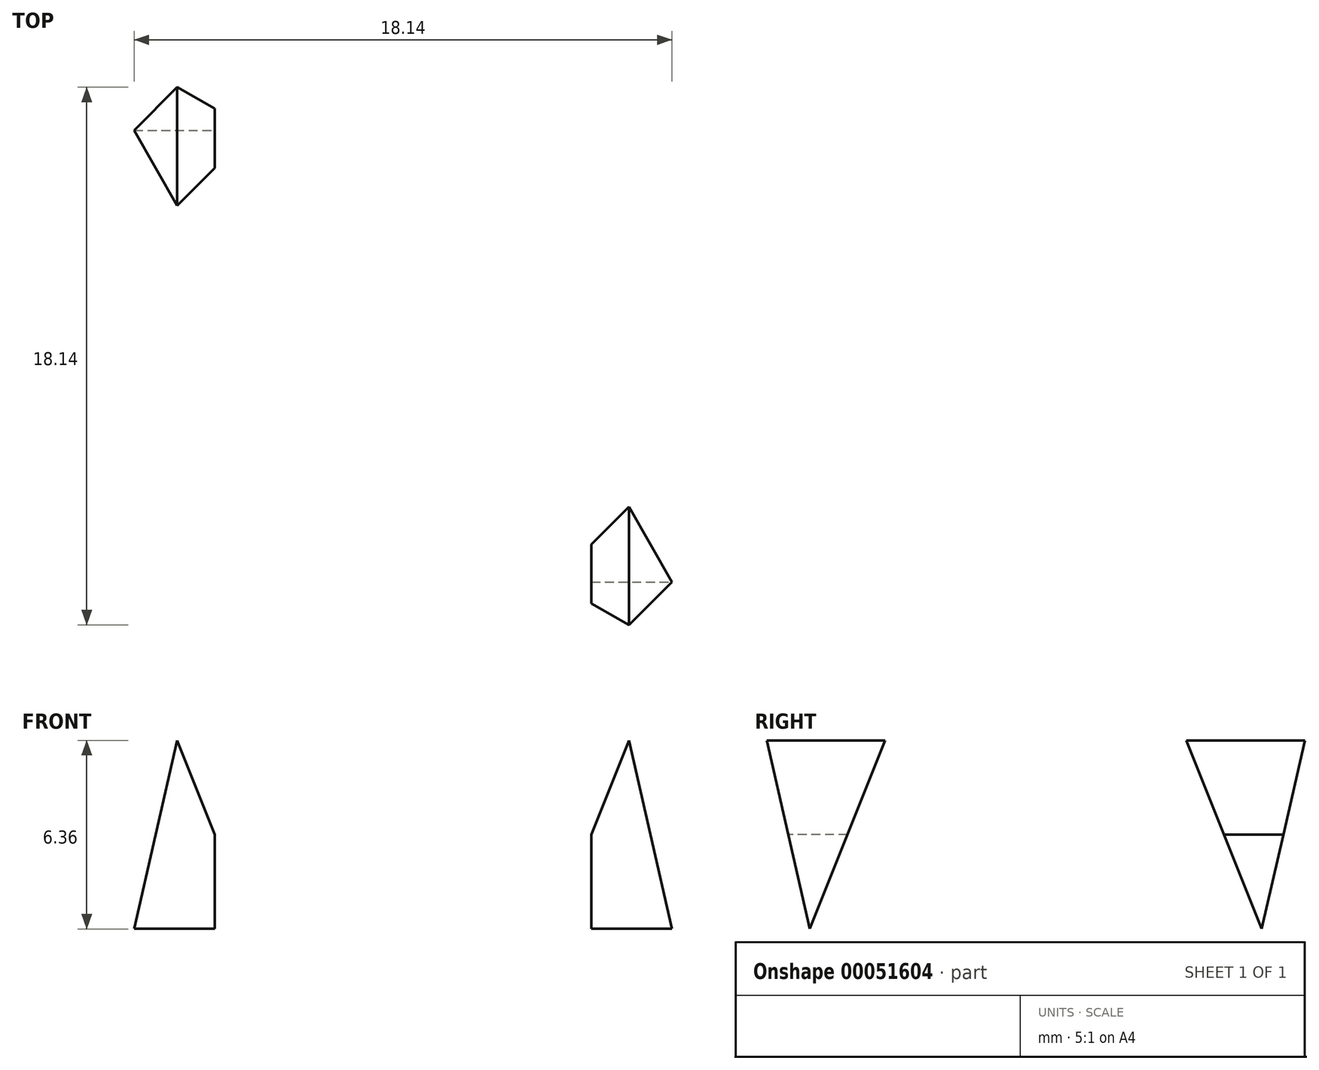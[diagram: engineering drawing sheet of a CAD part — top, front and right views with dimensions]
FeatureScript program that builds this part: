
annotation { "Feature Type Name" : "Feature", "Feature Type Description" : "" }
export const myFeature = defineFeature(function(context is Context, id is Id, definition is map)
    precondition{}
    {
        {
            var Q0;
            Q0=qCreatedBy(makeId("Front.planeOp"),FACE);
            var sketch = newSketch(context, id + "F0", { "sketchPlane" : qUnion([Q0])});
            skLineSegment(sketch, "E0", {"start": v(0, 0) * mm, "end": v(0, 38.1) * mm});
            skLineSegment(sketch, "E1", {"start": v(0, 38.1) * mm, "end": v(38.1, 38.1) * mm});
            skLineSegment(sketch, "E2", {"start": v(38.1, 38.1) * mm, "end": v(38.1, 0) * mm});
            skLineSegment(sketch, "E3", {"start": v(0, 0) * mm, "end": v(38.1, 0) * mm});
            skSolve(sketch);
        }
        {
            var Q0;
            Q0=makeQuery(id+"F0.imprint","IMPRINT",FACE,{"disambiguationData":[TD([[makeQuery(id+"F0.imprint","IMPRINT",EDGE,{"derivedFrom":sQuery(id+"F0.wireOp",EDGE,"E0")}),-1.0]])]});
            extrude(context, id + "F1", {"entities" : qUnion([Q0]), "depth" : 38.1 * mm});
        }
        {
            var Q0;
            Q0=qCreatedBy(makeId("Front.planeOp"),FACE);
            cPlane(context, id + "F2", {"entities" : qUnion([Q0]), "cplaneType" : CPlaneType.OFFSET, "offset" : 38.1 * mm, "width" : 152.4 * mm, "height" : 152.4 * mm});
        }
        {
            var Q0;
            Q0=qCreatedBy(makeId("Right.planeOp"),FACE);
            cPlane(context, id + "F3", {"entities" : qUnion([Q0]), "cplaneType" : CPlaneType.OFFSET, "offset" : 38.1 * mm, "width" : 152.4 * mm, "height" : 152.4 * mm});
        }
        {
            var Q0;
            Q0=qCreatedBy(makeId("Top.planeOp"),FACE);
            cPlane(context, id + "F4", {"entities" : qUnion([Q0]), "cplaneType" : CPlaneType.OFFSET, "offset" : 38.1 * mm, "width" : 152.4 * mm, "height" : 152.4 * mm});
        }
        {
            var Q0;
            Q0=qCreatedBy(id+"F3.planeOp",FACE);
            var sketch = newSketch(context, id + "F5", { "sketchPlane" : qUnion([Q0])});
            skLineSegment(sketch, "E4.bottom", {"start": v(0, 0) * mm, "end": v(-38.1, 0) * mm});
            skLineSegment(sketch, "E4.top", {"start": v(0, 38.1) * mm, "end": v(-38.1, 38.1) * mm});
            skLineSegment(sketch, "E4.left", {"start": v(0, 0) * mm, "end": v(0, 38.1) * mm});
            skLineSegment(sketch, "E4.right", {"start": v(-38.1, 0) * mm, "end": v(-38.1, 38.1) * mm});
            skLineSegment(sketch, "E5", {"start": v(-38.1, 38.1) * mm, "end": v(-31.75, 0) * mm});
            skLineSegment(sketch, "E6", {"start": v(-38.1, 38.1) * mm, "end": v(-31.75, 38.1) * mm});
            skLineSegment(sketch, "E7", {"start": v(-31.75, 38.1) * mm, "end": v(-26.67, 15.88) * mm});
            skLineSegment(sketch, "E8", {"start": v(-26.67, 15.88) * mm, "end": v(-21.6, 28.58) * mm});
            skLineSegment(sketch, "E9", {"start": v(-21.6, 28.58) * mm, "end": v(-16.51, 28.58) * mm});
            skLineSegment(sketch, "E10", {"start": v(-16.51, 28.58) * mm, "end": v(-11.43, 15.88) * mm});
            skLineSegment(sketch, "E11", {"start": v(-11.43, 15.88) * mm, "end": v(-6.35, 38.1) * mm});
            skLineSegment(sketch, "E12", {"start": v(-6.35, 38.1) * mm, "end": v(0, 38.1) * mm});
            skLineSegment(sketch, "E13", {"start": v(0, 38.1) * mm, "end": v(-6.35, 0) * mm});
            skLineSegment(sketch, "E14", {"start": v(-25.4, 0) * mm, "end": v(-19.05, 15.88) * mm});
            skLineSegment(sketch, "E15", {"start": v(-19.05, 15.88) * mm, "end": v(-12.7, 0) * mm});
            skLineSegment(sketch, "E16", {"start": v(-12.7, 0) * mm, "end": v(-6.35, 0) * mm});
            skLineSegment(sketch, "E17", {"start": v(-25.4, 0) * mm, "end": v(-31.75, 0) * mm});
            skSolve(sketch);
        }
        {
            var Q0;
            {var subQ0=sQuery(id+"F5.wireOp",EDGE,"E4.left");Q0=makeQuery(id+"F5.imprint","IMPRINT",FACE,{"disambiguationData":[TD([[makeQuery(id+"F5.imprint","IMPRINT",EDGE,{"derivedFrom":subQ0}),1.0]])]});}
            var Q1;
            {var subQ0=sQuery(id+"F5.wireOp",EDGE,"E14");Q1=makeQuery(id+"F5.imprint","IMPRINT",FACE,{"disambiguationData":[TD([[makeQuery(id+"F5.imprint","IMPRINT",EDGE,{"derivedFrom":subQ0}),-1.0]])]});}
            var Q2;
            {var subQ0=sQuery(id+"F5.wireOp",EDGE,"E4.right");Q2=makeQuery(id+"F5.imprint","IMPRINT",FACE,{"disambiguationData":[TD([[makeQuery(id+"F5.imprint","IMPRINT",EDGE,{"derivedFrom":subQ0}),-1.0]])]});}
            var Q3;
            Q3=makeQuery(id+"F5.imprint","IMPRINT",FACE,{"disambiguationData":[TD([[makeQuery(id+"F5.imprint","IMPRINT",EDGE,{"derivedFrom":sQuery(id+"F5.wireOp",EDGE,"E4.top")}),1.0]])]});
            extrude(context, id + "F6", {"entities" : qUnion([Q0, Q1, Q2, Q3]), "operationType" : NewBodyOperationType.REMOVE, "oppositeDirection" : true, "depth" : 38.1 * mm});
        }
        {
            var Q0;
            Q0=qCreatedBy(id+"F2.planeOp",FACE);
            var sketch = newSketch(context, id + "F7", { "sketchPlane" : qUnion([Q0])});
            skLineSegment(sketch, "E18.bottom", {"start": v(0, 0) * mm, "end": v(38.1, 0) * mm});
            skLineSegment(sketch, "E18.top", {"start": v(0, 38.1) * mm, "end": v(38.1, 38.1) * mm});
            skLineSegment(sketch, "E18.left", {"start": v(0, 0) * mm, "end": v(0, 38.1) * mm});
            skLineSegment(sketch, "E18.right", {"start": v(38.1, 0) * mm, "end": v(38.1, 38.1) * mm});
            skLineSegment(sketch, "E19", {"start": v(0, 0) * mm, "end": v(6.35, 38.1) * mm});
            skLineSegment(sketch, "E20", {"start": v(6.35, 38.1) * mm, "end": v(12.7, 38.1) * mm});
            skLineSegment(sketch, "E21", {"start": v(12.7, 38.1) * mm, "end": v(19.05, 22.23) * mm});
            skLineSegment(sketch, "E22", {"start": v(19.05, 22.23) * mm, "end": v(25.4, 38.1) * mm});
            skLineSegment(sketch, "E23", {"start": v(31.75, 38.1) * mm, "end": v(38.1, 0) * mm});
            skLineSegment(sketch, "E24", {"start": v(38.1, 0) * mm, "end": v(31.75, 0) * mm});
            skLineSegment(sketch, "E25", {"start": v(31.75, 0) * mm, "end": v(26.67, 22.22) * mm});
            skLineSegment(sketch, "E26", {"start": v(26.67, 22.22) * mm, "end": v(21.59, 9.53) * mm});
            skLineSegment(sketch, "E27", {"start": v(21.59, 9.53) * mm, "end": v(16.51, 9.53) * mm});
            skLineSegment(sketch, "E28", {"start": v(16.51, 9.52) * mm, "end": v(11.43, 22.22) * mm});
            skLineSegment(sketch, "E29", {"start": v(11.43, 22.22) * mm, "end": v(6.35, 0) * mm});
            skLineSegment(sketch, "E30", {"start": v(0, 0) * mm, "end": v(6.35, 0) * mm});
            skSolve(sketch);
        }
        {
            var Q0;
            {var subQ0=sQuery(id+"F7.wireOp",EDGE,"E18.left");Q0=makeQuery(id+"F7.imprint","IMPRINT",FACE,{"disambiguationData":[TD([[makeQuery(id+"F7.imprint","IMPRINT",EDGE,{"derivedFrom":subQ0}),-1.0]])]});}
            var Q1;
            Q1=makeQuery(id+"F7.imprint","IMPRINT",FACE,{"disambiguationData":[TD([[makeQuery(id+"F7.imprint","IMPRINT",EDGE,{"derivedFrom":sQuery(id+"F7.wireOp",EDGE,"E18.bottom")}),1.0]])]});
            var Q2;
            {var subQ0=sQuery(id+"F7.wireOp",EDGE,"E21");Q2=makeQuery(id+"F7.imprint","IMPRINT",FACE,{"disambiguationData":[TD([[makeQuery(id+"F7.imprint","IMPRINT",EDGE,{"derivedFrom":subQ0}),1.0]])]});}
            var Q3;
            {var subQ0=sQuery(id+"F7.wireOp",EDGE,"E18.right");Q3=makeQuery(id+"F7.imprint","IMPRINT",FACE,{"disambiguationData":[TD([[makeQuery(id+"F7.imprint","IMPRINT",EDGE,{"derivedFrom":subQ0}),1.0]])]});}
            extrude(context, id + "F8", {"entities" : qUnion([Q0, Q1, Q2, Q3]), "operationType" : NewBodyOperationType.REMOVE, "oppositeDirection" : true, "depth" : 38.1 * mm});
        }
        {
            var Q0;
            Q0=qCreatedBy(id+"F4.planeOp",FACE);
            var sketch = newSketch(context, id + "F9", { "sketchPlane" : qUnion([Q0])});
            skLineSegment(sketch, "E31.bottom", {"start": v(0, -38.1) * mm, "end": v(38.1, -38.1) * mm});
            skLineSegment(sketch, "E31.top", {"start": v(0, 0) * mm, "end": v(38.1, 0) * mm});
            skLineSegment(sketch, "E31.left", {"start": v(0, -38.1) * mm, "end": v(0, 0) * mm});
            skLineSegment(sketch, "E31.right", {"start": v(38.1, -38.1) * mm, "end": v(38.1, 0) * mm});
            skLineSegment(sketch, "E32", {"start": v(38.1, -7.62) * mm, "end": v(12.7, -7.62) * mm});
            skLineSegment(sketch, "E33", {"start": v(12.7, -7.62) * mm, "end": v(12.7, -15.24) * mm});
            skLineSegment(sketch, "E34", {"start": v(12.7, -15.24) * mm, "end": v(38.1, -15.24) * mm});
            skLineSegment(sketch, "E35", {"start": v(0, -22.86) * mm, "end": v(25.4, -22.86) * mm});
            skLineSegment(sketch, "E36", {"start": v(25.4, -22.86) * mm, "end": v(25.4, -30.48) * mm});
            skLineSegment(sketch, "E37", {"start": v(25.4, -30.48) * mm, "end": v(0, -30.48) * mm});
            skSolve(sketch);
        }
        {
            var Q0;
            {var subQ0=sQuery(id+"F9.wireOp",EDGE,"E32");Q0=makeQuery(id+"F9.imprint","IMPRINT",FACE,{"disambiguationData":[TD([[makeQuery(id+"F9.imprint","IMPRINT",EDGE,{"derivedFrom":subQ0}),1.0]])]});}
            var Q1;
            {var subQ0=sQuery(id+"F9.wireOp",EDGE,"E35");Q1=makeQuery(id+"F9.imprint","IMPRINT",FACE,{"disambiguationData":[TD([[makeQuery(id+"F9.imprint","IMPRINT",EDGE,{"derivedFrom":subQ0}),-1.0]])]});}
            extrude(context, id + "F10", {"entities" : qUnion([Q0, Q1]), "operationType" : NewBodyOperationType.REMOVE, "oppositeDirection" : true, "depth" : 38.1 * mm});
        }
    });
